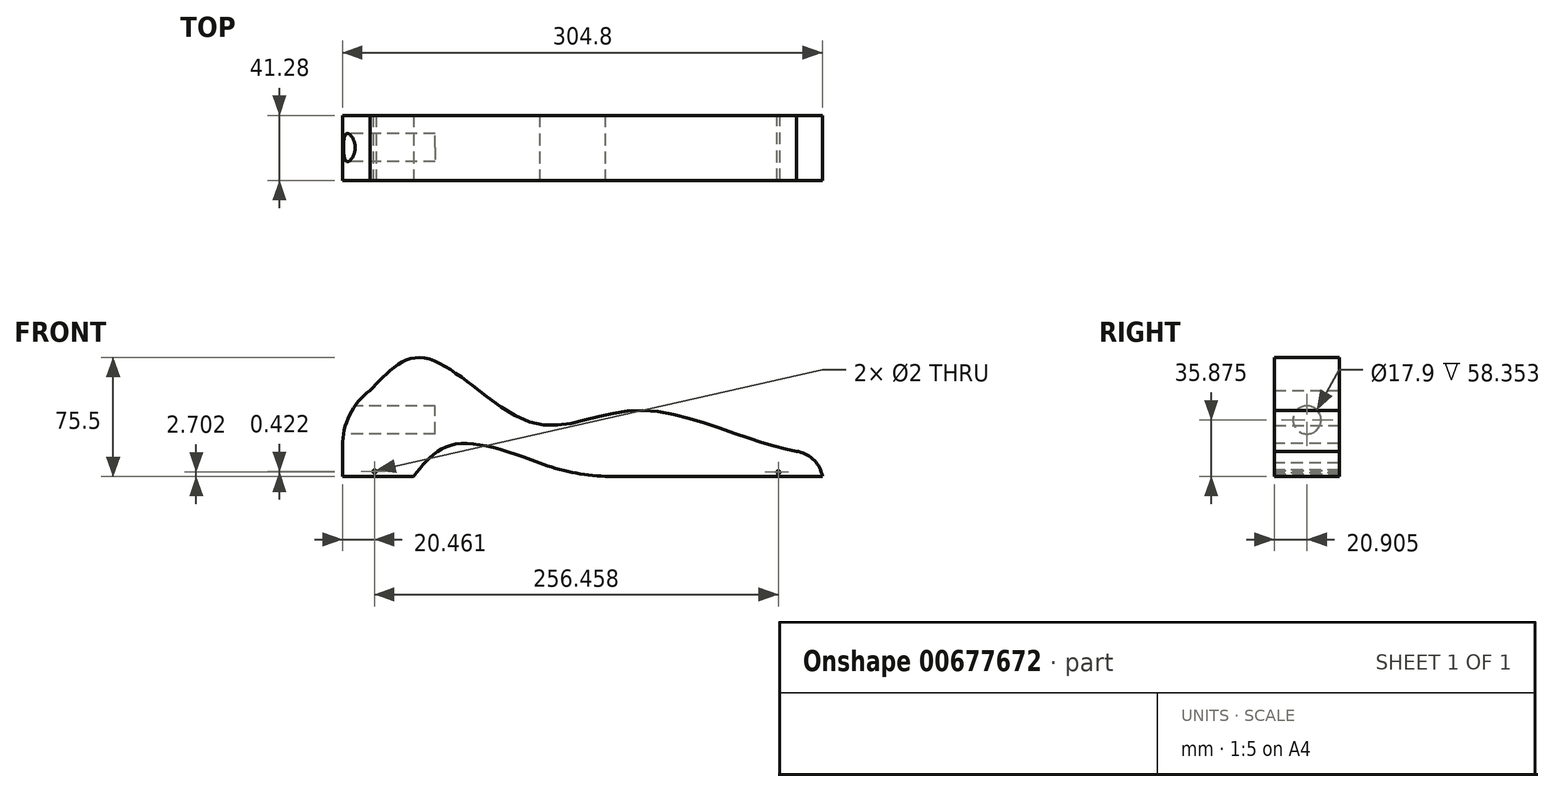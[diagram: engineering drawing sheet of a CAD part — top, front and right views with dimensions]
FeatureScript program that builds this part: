
annotation { "Feature Type Name" : "Feature", "Feature Type Description" : "" }
export const myFeature = defineFeature(function(context is Context, id is Id, definition is map)
    precondition{}
    {
        {
            var Q0;
            Q0=qCreatedBy(makeId("Front.planeOp"),FACE);
            var sketch = newSketch(context, id + "F0", { "sketchPlane" : qUnion([Q0])});
            skLineSegment(sketch, "E0", {"start": v(0, 0) * mm, "end": v(304.8, 0) * mm});
            skLineSegment(sketch, "E1", {"start": v(304.8, 0) * mm, "end": v(304.8, 12.7) * mm});
            skLineSegment(sketch, "E2", {"start": v(304.8, 12.7) * mm, "end": v(0, 73.03) * mm});
            skLineSegment(sketch, "E3", {"start": v(0, 73.03) * mm, "end": v(0, 0) * mm});
            skSolve(sketch);
        }
        {
            var Q0;
            Q0=makeQuery(id+"F0.imprint","IMPRINT",FACE,{"disambiguationData":[TD([[makeQuery(id+"F0.imprint","IMPRINT",EDGE,{"derivedFrom":sQuery(id+"F0.wireOp",EDGE,"E0")}),1.0]])]});
            extrude(context, id + "F1", {"entities" : qUnion([Q0]), "oppositeDirection" : true, "depth" : 41.27 * mm, "offsetDistance" : 25.4 * mm});
        }
        {
            var Q0;
            Q0=makeQuery(id+"F1.opExtrude","CAP_FACE",FACE,{"disambiguationData":[OSD([sQuery(id+"F0.wireOp",EDGE,"E0"),sQuery(id+"F0.wireOp",EDGE,"E1"),sQuery(id+"F0.wireOp",EDGE,"E2"),sQuery(id+"F0.wireOp",EDGE,"E3")])],"isStart":true});
            var sketch = newSketch(context, id + "F2", { "sketchPlane" : qUnion([Q0])});
            skLineSegment(sketch, "E4", {"start": v(0, 42.37) * mm, "end": v(49.97, 63.14) * mm});
            skSolve(sketch);
        }
        {
            var Q0;
            {var subQ0=sQuery(id+"F2.wireOp",EDGE,"E4");Q0=makeQuery(id+"F2.imprint","IMPRINT",FACE,{"disambiguationData":[TD([[makeQuery(id+"F2.imprint","IMPRINT",EDGE,{"derivedFrom":subQ0}),1.0]])]});}
            extrude(context, id + "F3", {"entities" : qUnion([Q0]), "operationType" : NewBodyOperationType.REMOVE, "oppositeDirection" : true, "depth" : 76.2 * mm, "offsetDistance" : 25.4 * mm});
        }
        {
            var Q0;
            Q0=makeQuery(id+"F1.opExtrude","CAP_FACE",FACE,{"disambiguationData":[OSD([sQuery(id+"F0.wireOp",EDGE,"E0"),sQuery(id+"F0.wireOp",EDGE,"E1"),sQuery(id+"F0.wireOp",EDGE,"E2"),sQuery(id+"F0.wireOp",EDGE,"E3")])],"isStart":true});
            var sketch = newSketch(context, id + "F4", { "sketchPlane" : qUnion([Q0])});
            skFitSpline(sketch, "E5", {"points": [v(0, 42.37) * mm, v(49.97, 63.14) * mm, v(118.04, 42.37) * mm, v(182.58, 36.89) * mm, v(304.8, 12.7) * mm], "startDerivative": vector(224.98, 150.18) * mm, "endDerivative": vector(415.88, -100.84) * mm});
            skLineSegment(sketch, "E6", {"start": v(49.97, 63.14) * mm, "end": v(182.58, 36.89) * mm});
            skLineSegment(sketch, "E7", {"start": v(49.97, 63.14) * mm, "end": v(73.44, 58.49) * mm});
            skSolve(sketch);
        }
        {
            var Q0;
            Q0 = qSketchRegion(id + "F4", true);
            extrude(context, id + "F5", {"entities" : qUnion([Q0]), "operationType" : NewBodyOperationType.REMOVE, "oppositeDirection" : true, "depth" : 76.2 * mm, "offsetDistance" : 25.4 * mm});
        }
        {
            var Q0;
            Q0=makeQuery(id+"F1.opExtrude","CAP_FACE",FACE,{"disambiguationData":[OSD([sQuery(id+"F0.wireOp",EDGE,"E0"),sQuery(id+"F0.wireOp",EDGE,"E1"),sQuery(id+"F0.wireOp",EDGE,"E2"),sQuery(id+"F0.wireOp",EDGE,"E3")])],"isStart":true});
            var sketch = newSketch(context, id + "F6", { "sketchPlane" : qUnion([Q0])});
            skLineSegment(sketch, "E8", {"start": v(0, 42.37) * mm, "end": v(73.44, 58.49) * mm});
            skSolve(sketch);
        }
        {
            var Q0;
            Q0=makeQuery(id+"F6.imprint","IMPRINT",FACE,{"disambiguationData":[TD([[makeQuery(id+"F6.imprint","IMPRINT",EDGE,{"derivedFrom":sQuery(id+"F6.wireOp",EDGE,"E8")}),1.0]])]});
            extrude(context, id + "F7", {"entities" : qUnion([Q0]), "operationType" : NewBodyOperationType.ADD, "depth" : 76.2 * mm, "offsetDistance" : 25.4 * mm});
        }
        {
            var Q0;
            Q0=makeQuery(id+"F7.opExtrude","CAP_FACE",FACE,{"disambiguationData":[OSD([sQuery(id+"F0.wireOp",EDGE,"E2"),sQuery(id+"F2.wireOp",EDGE,"E4"),sQuery(id+"F6.wireOp",EDGE,"E8")])],"isStart":false});
            extrude(context, id + "F8", {"entities" : qUnion([Q0]), "operationType" : NewBodyOperationType.REMOVE, "oppositeDirection" : true, "depth" : 76.2 * mm, "offsetDistance" : 25.4 * mm});
        }
        {
            var Q0;
            {var subQ0=sQuery(id+"F0.wireOp",EDGE,"E2");Q0=makeQuery(id+"F8.boolean.opBoolean","MERGE",FACE,{"derivedFrom":[makeQuery(id+"F1.opExtrude","CAP_FACE",FACE,{"disambiguationData":[OSD([sQuery(id+"F0.wireOp",EDGE,"E0"),sQuery(id+"F0.wireOp",EDGE,"E1"),subQ0,sQuery(id+"F0.wireOp",EDGE,"E3")])],"isStart":true}),makeQuery(id+"F8.opExtrude","CAP_FACE",FACE,{"disambiguationData":[OSD([subQ0,sQuery(id+"F2.wireOp",EDGE,"E4"),sQuery(id+"F6.wireOp",EDGE,"E8")])],"isStart":false})]});}
            var sketch = newSketch(context, id + "F9", { "sketchPlane" : qUnion([Q0])});
            skSolve(sketch);
        }
        {
            var Q0;
            {var subQ7=sQuery(id+"F0.wireOp",EDGE,"E0");Q0=makeQuery(id+"F9.imprint","IMPRINT",FACE,{"disambiguationData":[TD([[makeQuery(id+"F9.imprint","IMPRINT",EDGE,{"derivedFrom":makeQuery(id+"F1.opExtrude","CAP_EDGE",EDGE,{"disambiguationData":[OSD([subQ7])],"isStart":true})}),1.0]])]});}
            var sketch = newSketch(context, id + "F10", { "sketchPlane" : qUnion([Q0])});
            skFitSpline(sketch, "E9.0.0", {"points": [v(304.8, 12.7) * mm, v(260.6, 23.42) * mm, v(184.51, 41.87) * mm, v(119.37, 34.45) * mm, v(49.6, 75.48) * mm, v(15.76, 52.9) * mm, v(0, 42.37) * mm]});
            skLineSegment(sketch, "E9.0.1", {"start": v(73.44, 58.49) * mm, "end": v(49.97, 63.14) * mm});
            skLineSegment(sketch, "E9.0.2", {"start": v(49.97, 63.14) * mm, "end": v(0, 42.37) * mm});
            skLineSegment(sketch, "E9.0.3", {"start": v(0, 42.37) * mm, "end": v(0, 0) * mm});
            skLineSegment(sketch, "E9.0.4", {"start": v(0, 0) * mm, "end": v(304.8, 0) * mm});
            skLineSegment(sketch, "E9.0.5", {"start": v(304.8, 0) * mm, "end": v(304.8, 12.7) * mm});
            skLineSegment(sketch, "E9.0.6", {"start": v(304.8, 12.7) * mm, "end": v(182.58, 36.89) * mm});
            skArc(sketch, "E10", {"start": v(98.75, 48.94) * mm, "mid": v(48.22, 63.04) * mm, "end": v(0, 42.37) * mm});
            skSolve(sketch);
        }
        {
            var Q0;
            Q0 = qSketchRegion(id + "F10", true);
            extrude(context, id + "F11", {"entities" : qUnion([Q0]), "operationType" : NewBodyOperationType.ADD, "depth" : 41.27 * mm, "offsetDistance" : 25.4 * mm});
        }
        {
            var Q0;
            Q0=makeQuery(id+"F11.opExtrude","CAP_FACE",FACE,{"disambiguationData":[OSD([sQuery(id+"F10.wireOp",EDGE,"E9.0.0"),sQuery(id+"F10.wireOp",EDGE,"E9.0.3"),sQuery(id+"F10.wireOp",EDGE,"E9.0.4"),sQuery(id+"F10.wireOp",EDGE,"E9.0.5"),sQuery(id+"F10.wireOp",EDGE,"E9.0.6"),sQuery(id+"F10.wireOp",EDGE,"E10")])],"isStart":false});
            var sketch = newSketch(context, id + "F12", { "sketchPlane" : qUnion([Q0])});
            skFitSpline(sketch, "E11", {"points": [v(45.28, 0) * mm, v(70.43, 20.21) * mm, v(145.9, 0) * mm], "startDerivative": vector(52.62, 68.26) * mm, "endDerivative": vector(142.12, -59.03) * mm});
            skSolve(sketch);
        }
        {
            var Q0;
            Q0 = qSketchRegion(id + "F12", true);
            var Q1;
            {var subQ0=sQuery(id+"F12.wireOp",EDGE,"E11");Q1=makeQuery(id+"F12.imprint","IMPRINT",FACE,{"disambiguationData":[TD([[makeQuery(id+"F12.imprint","IMPRINT",EDGE,{"derivedFrom":subQ0}),-1.0]])]});}
            extrude(context, id + "F13", {"entities" : qUnion([Q0, Q1]), "operationType" : NewBodyOperationType.REMOVE, "oppositeDirection" : true, "depth" : 76.2 * mm, "offsetDistance" : 25.4 * mm});
        }
        {
            var Q0;
            Q0=makeQuery(id+"F11.opExtrude","CAP_FACE",FACE,{"disambiguationData":[OSD([sQuery(id+"F10.wireOp",EDGE,"E9.0.0"),sQuery(id+"F10.wireOp",EDGE,"E9.0.3"),sQuery(id+"F10.wireOp",EDGE,"E9.0.4"),sQuery(id+"F10.wireOp",EDGE,"E9.0.5"),sQuery(id+"F10.wireOp",EDGE,"E9.0.6"),sQuery(id+"F10.wireOp",EDGE,"E10")])],"isStart":false});
            var sketch = newSketch(context, id + "F14", { "sketchPlane" : qUnion([Q0])});
            skArc(sketch, "E12", {"start": v(125.35, 8.38) * mm, "mid": v(152.12, 1.48) * mm, "end": v(179.73, 0) * mm});
            skSolve(sketch);
        }
        {
            var Q0;
            Q0 = qSketchRegion(id + "F14", true);
            var Q1;
            {var subQ0=sQuery(id+"F14.wireOp",EDGE,"E12");var subQ1=sQuery(id+"F12.wireOp",EDGE,"E11");var subQ2=makeQuery(id+"F13.boolean.opBoolean","COPY",EDGE,{"derivedFrom":makeQuery(id+"F13.opExtrude","CAP_EDGE",EDGE,{"disambiguationData":[OSD([subQ1])],"isStart":true})});var subQ3=makeQuery(id+"F14.imprint","INTERSECT",VERTEX,{"derivedFrom":[subQ2,subQ0]});Q1=makeQuery(id+"F14.imprint","IMPRINT",FACE,{"disambiguationData":[TD([[makeQuery(id+"F14.imprint","IMPRINT",EDGE,{"disambiguationData":[TD([[subQ3,-1.0]])],"derivedFrom":subQ0}),-1.0]])]});}
            extrude(context, id + "F15", {"entities" : qUnion([Q0, Q1]), "operationType" : NewBodyOperationType.ADD, "depth" : 25.4 * mm, "offsetDistance" : 25.4 * mm});
        }
        {
            var Q0;
            Q0 = qSketchRegion(id + "FqBPXuE1PWNQ8oF_1", true);
            var Q1;
            Q1=makeQuery(id+"F15.opExtrude","CAP_FACE",FACE,{"disambiguationData":[OSD([sQuery(id+"F10.wireOp",EDGE,"E9.0.4"),sQuery(id+"F12.wireOp",EDGE,"E11"),sQuery(id+"F14.wireOp",EDGE,"E12")])],"isStart":false});
            extrude(context, id + "F16", {"entities" : qUnion([Q0, Q1]), "operationType" : NewBodyOperationType.REMOVE, "oppositeDirection" : true, "depth" : 76.2 * mm, "offsetDistance" : 25.4 * mm});
        }
        {
            var Q0;
            Q0=makeQuery(id+"F1.opExtrude","CAP_FACE",FACE,{"disambiguationData":[OSD([sQuery(id+"F0.wireOp",EDGE,"E0"),sQuery(id+"F0.wireOp",EDGE,"E1"),sQuery(id+"F0.wireOp",EDGE,"E2"),sQuery(id+"F0.wireOp",EDGE,"E3")])],"isStart":false});
            var sketch = newSketch(context, id + "F17", { "sketchPlane" : qUnion([Q0])});
            skArc(sketch, "E13", {"start": v(0, 42.37) * mm, "mid": v(-47.03, 62.97) * mm, "end": v(-96.65, 49.76) * mm});
            skSolve(sketch);
        }
        {
            var Q0;
            {var subQ4=sQuery(id+"F0.wireOp",EDGE,"E0");Q0=makeQuery(id+"F17.imprint","IMPRINT",FACE,{"disambiguationData":[TD([[makeQuery(id+"F17.imprint","IMPRINT",EDGE,{"derivedFrom":makeQuery(id+"F1.opExtrude","CAP_EDGE",EDGE,{"disambiguationData":[OSD([subQ4])],"isStart":false})}),-1.0]])]});}
            var Q1;
            {var subQ2=sQuery(id+"F10.wireOp",EDGE,"E10");var subQ3=sQuery(id+"F10.wireOp",EDGE,"E9.0.3");var subQ4=makeQuery(id+"F11.opExtrude","CAP_FACE",FACE,{"disambiguationData":[OSD([sQuery(id+"F10.wireOp",EDGE,"E9.0.0"),subQ3,sQuery(id+"F10.wireOp",EDGE,"E9.0.4"),sQuery(id+"F10.wireOp",EDGE,"E9.0.5"),sQuery(id+"F10.wireOp",EDGE,"E9.0.6"),subQ2])],"isStart":true});Q1=makeQuery(id+"F11.boolean.opBoolean","SPLIT",FACE,{"disambiguationData":[TD([makeQuery(id+"F1.opExtrude","SWEPT_FACE",FACE,{"disambiguationData":[OSD([sQuery(id+"F0.wireOp",EDGE,"E3")])]})])],"derivedFrom":subQ4});}
            extrude(context, id + "F18", {"entities" : qUnion([Q0]), "operationType" : NewBodyOperationType.REMOVE, "endBound" : BoundingType.UP_TO_SURFACE, "oppositeDirection" : true, "depth" : 25.4 * mm, "endBoundEntityFace" : qUnion([Q1]), "offsetDistance" : 25.4 * mm});
        }
        {
            var Q0;
            Q0=makeQuery(id+"F11.boolean.opBoolean","MERGE",EDGE,{"derivedFrom":[makeQuery(id+"F1.opExtrude","SWEPT_EDGE",EDGE,{"disambiguationData":[OSD([sQuery(id+"F0.wireOp",EDGE,"E1"),sQuery(id+"F0.wireOp",EDGE,"E2")])]}),makeQuery(id+"F11.opExtrude","SWEPT_EDGE",EDGE,{"disambiguationData":[OSD([sQuery(id+"F10.wireOp",EDGE,"E9.0.5"),sQuery(id+"F10.wireOp",EDGE,"E9.0.6")])]})]});
            fillet(context, id + "F19", {"entities" : qUnion([Q0]), "radius" : 19 * mm, "tangentPropagation" : true, "allowEdgeOverflow" : false});
        }
        {
            var Q0;
            Q0=makeQuery(id+"F11.opExtrude","SWEPT_EDGE",EDGE,{"disambiguationData":[OSD([sQuery(id+"F10.wireOp",EDGE,"E9.0.2"),sQuery(id+"F10.wireOp",EDGE,"E9.0.3"),sQuery(id+"F10.wireOp",EDGE,"E10")])]});
            fillet(context, id + "F20", {"entities" : qUnion([Q0]), "radius" : 44.12 * mm, "tangentPropagation" : true, "allowEdgeOverflow" : false});
        }
        {
            var Q0;
            Q0=makeQuery(id+"F11.opExtrude","CAP_FACE",FACE,{"disambiguationData":[OSD([sQuery(id+"F10.wireOp",EDGE,"E9.0.0"),sQuery(id+"F10.wireOp",EDGE,"E9.0.3"),sQuery(id+"F10.wireOp",EDGE,"E9.0.4"),sQuery(id+"F10.wireOp",EDGE,"E9.0.5"),sQuery(id+"F10.wireOp",EDGE,"E9.0.6"),sQuery(id+"F10.wireOp",EDGE,"E10")])],"isStart":false});
            var sketch = newSketch(context, id + "F21", { "sketchPlane" : qUnion([Q0])});
            skCircle(sketch, "E14", {"center": v(20.46, 3.12) * mm, "radius": 1 * mm});
            skSolve(sketch);
        }
        {
            var Q0;
            Q0=makeQuery(id+"F21.imprint","IMPRINT",FACE,{"disambiguationData":[TD([[makeQuery(id+"F21.imprint","IMPRINT",EDGE,{"derivedFrom":sQuery(id+"F21.wireOp",EDGE,"E14")}),1.0]])]});
            extrude(context, id + "F22", {"entities" : qUnion([Q0]), "operationType" : NewBodyOperationType.REMOVE, "oppositeDirection" : true, "depth" : 38.5 * mm, "offsetDistance" : 25 * mm});
        }
        {
            var Q0;
            Q0=makeQuery(id+"F22.boolean.opBoolean","COPY",FACE,{"derivedFrom":makeQuery(id+"F22.opExtrude","CAP_FACE",FACE,{"disambiguationData":[OSD([sQuery(id+"F21.wireOp",EDGE,"E14")])],"isStart":false})});
            extrude(context, id + "F23", {"entities" : qUnion([Q0]), "operationType" : NewBodyOperationType.REMOVE, "oppositeDirection" : true, "depth" : 25 * mm, "offsetDistance" : 25 * mm});
        }
        {
            var Q0;
            {var subQ7=sQuery(id+"F0.wireOp",EDGE,"E0");Q0=makeQuery(id+"F9.imprint","IMPRINT",FACE,{"disambiguationData":[TD([[makeQuery(id+"F9.imprint","IMPRINT",EDGE,{"derivedFrom":makeQuery(id+"F1.opExtrude","CAP_EDGE",EDGE,{"disambiguationData":[OSD([subQ7])],"isStart":true})}),1.0]])]});}
            var sketch = newSketch(context, id + "F24", { "sketchPlane" : qUnion([Q0])});
            skCircle(sketch, "E15", {"center": v(276.92, 2.7) * mm, "radius": 1 * mm});
            skSolve(sketch);
        }
        {
            var Q0;
            Q0 = qSketchRegion(id + "F24", true);
            extrude(context, id + "F25", {"entities" : qUnion([Q0]), "operationType" : NewBodyOperationType.REMOVE, "depth" : 56.1 * mm, "offsetDistance" : 25 * mm});
        }
        {
            var Q0;
            Q0=qCreatedBy(makeId("Right.planeOp"),FACE);
            var sketch = newSketch(context, id + "F26", { "sketchPlane" : qUnion([Q0])});
            skCircle(sketch, "E16", {"center": v(-20.38, 35.88) * mm, "radius": 8.95 * mm});
            skSolve(sketch);
        }
        {
            var Q0;
            Q0=makeQuery(id+"F26.imprint","IMPRINT",FACE,{"disambiguationData":[TD([[makeQuery(id+"F26.imprint","IMPRINT",EDGE,{"derivedFrom":sQuery(id+"F26.wireOp",EDGE,"E16")}),1.0]])]});
            extrude(context, id + "F27", {"entities" : qUnion([Q0]), "operationType" : NewBodyOperationType.REMOVE, "depth" : 59 * mm, "offsetDistance" : 25 * mm});
        }
    });
